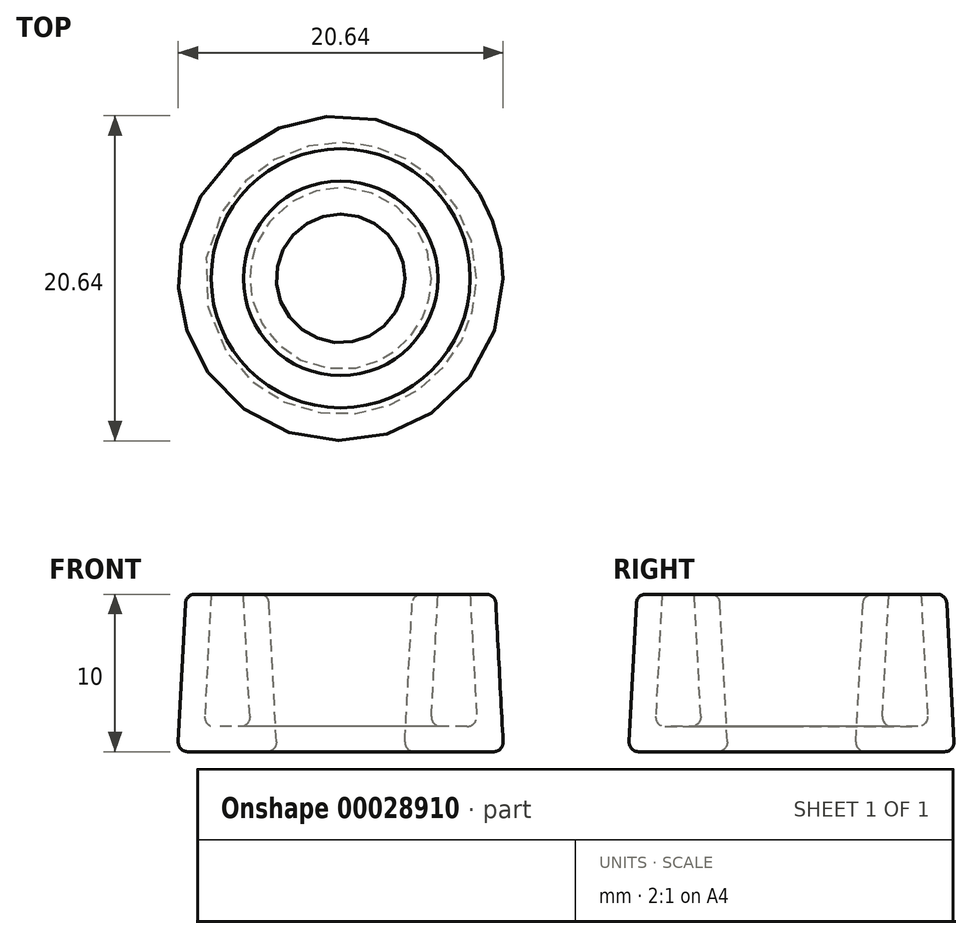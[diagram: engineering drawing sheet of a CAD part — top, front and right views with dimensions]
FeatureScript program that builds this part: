
annotation { "Feature Type Name" : "Feature", "Feature Type Description" : "" }
export const myFeature = defineFeature(function(context is Context, id is Id, definition is map)
    precondition{}
    {
        {
            var Q0;
            Q0=qCreatedBy(makeId("Top.planeOp"),FACE);
            var sketch = newSketch(context, id + "F0", { "sketchPlane" : qUnion([Q0])});
            skCircle(sketch, "E0", {"center": v(0, -10.65) * mm, "radius": 10.35 * mm});
            skCircle(sketch, "E1", {"center": v(0, -10.65) * mm, "radius": 4.05 * mm});
            skSolve(sketch);
        }
        {
            var Q0;
            Q0=makeQuery(id+"F0.imprint","IMPRINT",FACE,{"disambiguationData":[TD([[makeQuery(id+"F0.imprint","IMPRINT",EDGE,{"derivedFrom":sQuery(id+"F0.wireOp",EDGE,"e6d2bad5-9e76-4b41-926a-4b8b29525619")}),1.0]])]});
            var Q1;
            Q1=makeQuery(id+"F0.imprint","IMPRINT",FACE,{"disambiguationData":[TD([[makeQuery(id+"F0.imprint","IMPRINT",EDGE,{"derivedFrom":sQuery(id+"F0.wireOp",EDGE,"E0")}),1.0]])]});
            var Q2;
            Q2=makeQuery(id+"F0.imprint","IMPRINT",FACE,{"disambiguationData":[TD([[makeQuery(id+"F0.imprint","IMPRINT",EDGE,{"derivedFrom":sQuery(id+"F0.wireOp",EDGE,"abde0cf9-1f83-4301-beb9-ac4b5f17cbbd.bottom")}),1.0]])]});
            var Q3;
            Q3=makeQuery(id+"F0.imprint","IMPRINT",FACE,{"disambiguationData":[TD([[makeQuery(id+"F0.imprint","IMPRINT",EDGE,{"derivedFrom":sQuery(id+"F0.wireOp",EDGE,"26bd8618-c4e7-439a-99f6-bb982ce9a2120.MirrorC")}),-1.0]])]});
            var Q4;
            Q4=makeQuery(id+"F0.imprint","IMPRINT",FACE,{"disambiguationData":[TD([[makeQuery(id+"F0.imprint","IMPRINT",EDGE,{"derivedFrom":sQuery(id+"F0.wireOp",EDGE,"45c0c035-0ba1-440d-91dd-f4deb18173680.MirrorC")}),-1.0]])]});
            var Q5;
            Q5=makeQuery(id+"F0.imprint","IMPRINT",FACE,{"disambiguationData":[TD([[makeQuery(id+"F0.imprint","IMPRINT",EDGE,{"derivedFrom":sQuery(id+"F0.wireOp",EDGE,"92f10646-9b55-488a-b265-364474158b900.MirrorCS")}),1.0]])]});
            var Q6;
            {var subQ4=sQuery(id+"F0.wireOp",EDGE,"621f7957-7ed0-4eb6-82c1-ad9769d9a6c72.MirrorCS");Q6=makeQuery(id+"F0.imprint","IMPRINT",FACE,{"disambiguationData":[TD([[makeQuery(id+"F0.imprint","IMPRINT",EDGE,{"derivedFrom":subQ4}),-1.0]])]});}
            var Q7;
            Q7=makeQuery(id+"F0.imprint","IMPRINT",FACE,{"disambiguationData":[TD([[makeQuery(id+"F0.imprint","IMPRINT",EDGE,{"derivedFrom":sQuery(id+"F0.wireOp",EDGE,"621f7957-7ed0-4eb6-82c1-ad9769d9a6c70.MirrorCS")}),-1.0]])]});
            var Q8;
            Q8=makeQuery(id+"F0.imprint","IMPRINT",FACE,{"disambiguationData":[TD([[makeQuery(id+"F0.imprint","IMPRINT",EDGE,{"derivedFrom":sQuery(id+"F0.wireOp",EDGE,"621f7957-7ed0-4eb6-82c1-ad9769d9a6c78.MirrorCS")}),1.0]])]});
            var Q9;
            {var subQ4=sQuery(id+"F0.wireOp",EDGE,"621f7957-7ed0-4eb6-82c1-ad9769d9a6c72.MirrorCS");Q9=makeQuery(id+"F0.imprint","IMPRINT",FACE,{"disambiguationData":[TD([[makeQuery(id+"F0.imprint","IMPRINT",EDGE,{"derivedFrom":subQ4}),1.0]])]});}
            var Q10;
            Q10=makeQuery(id+"F0.imprint","IMPRINT",FACE,{"disambiguationData":[TD([[makeQuery(id+"F0.imprint","IMPRINT",EDGE,{"derivedFrom":sQuery(id+"F0.wireOp",EDGE,"0d3d05c0-9ec0-42d6-8d1c-98659f42b2b8.bottom")}),1.0]])]});
            var Q11;
            Q11=makeQuery(id+"F0.imprint","IMPRINT",FACE,{"disambiguationData":[TD([[makeQuery(id+"F0.imprint","IMPRINT",EDGE,{"derivedFrom":sQuery(id+"F0.wireOp",EDGE,"0d3d05c0-9ec0-42d6-8d1c-98659f42b2b8.bottom")}),1.0]])]});
            extrude(context, id + "F1", {"entities" : qUnion([Q0, Q1, Q2, Q3, Q4, Q5, Q6, Q7, Q8, Q9, Q10, Q11]), "depth" : 10 * mm, "hasDraft" : true, "draftAngle" : 3 * degree, "draftPullDirection" : true});
        }
        {
            var Q0;
            Q0=makeQuery(id+"F1.opExtrude","CAP_FACE",FACE,{"disambiguationData":[OSD([sQuery(id+"F0.wireOp",EDGE,"e6d2bad5-9e76-4b41-926a-4b8b29525619"),sQuery(id+"F0.wireOp",EDGE,"27f1a8c6-9d11-4593-bfca-9de2c4382994")])],"isStart":false});
            var Q1;
            Q1=makeQuery(id+"F1.opExtrude","CAP_FACE",FACE,{"disambiguationData":[OSD([sQuery(id+"F0.wireOp",EDGE,"b8262d11-0ced-4fc4-a484-381bc9a378e90.MirrorC"),sQuery(id+"F0.wireOp",EDGE,"9f1c5b67-5bd7-481e-852a-bcdd96d4567a0.MirrorC")])],"isStart":false});
            var Q2;
            Q2=makeQuery(id+"F1.opExtrude","CAP_FACE",FACE,{"disambiguationData":[OSD([sQuery(id+"F0.wireOp",EDGE,"E0"),sQuery(id+"F0.wireOp",EDGE,"E1")])],"isStart":false});
            var Q3;
            Q3=makeQuery(id+"F1.opExtrude","CAP_FACE",FACE,{"disambiguationData":[OSD([sQuery(id+"F0.wireOp",EDGE,"abde0cf9-1f83-4301-beb9-ac4b5f17cbbd.bottom"),sQuery(id+"F0.wireOp",EDGE,"abde0cf9-1f83-4301-beb9-ac4b5f17cbbd.top"),sQuery(id+"F0.wireOp",EDGE,"abde0cf9-1f83-4301-beb9-ac4b5f17cbbd.left"),sQuery(id+"F0.wireOp",EDGE,"abde0cf9-1f83-4301-beb9-ac4b5f17cbbd.right"),sQuery(id+"F0.wireOp",EDGE,"7a9050d6-7617-46cd-b5c2-3b15425381b2"),sQuery(id+"F0.wireOp",EDGE,"b158f154-8a0c-48af-83f9-a2040f8c14ea"),sQuery(id+"F0.wireOp",EDGE,"6b9fe175-4e1e-497c-82d7-d758e1c653ef.filletArc"),sQuery(id+"F0.wireOp",EDGE,"f33478da-a012-4289-b0bd-afe5d81a5774.filletArc"),sQuery(id+"F0.wireOp",EDGE,"24f43b8c-777b-4e50-8554-e1c6360b9280.filletArc"),sQuery(id+"F0.wireOp",EDGE,"1f811094-0bca-45d6-932f-2b620bfc63b1.filletArc")])],"isStart":false});
            var Q4;
            Q4=makeQuery(id+"F1.opExtrude","CAP_FACE",FACE,{"disambiguationData":[OSD([sQuery(id+"F0.wireOp",EDGE,"92f10646-9b55-488a-b265-364474158b900.MirrorCS"),sQuery(id+"F0.wireOp",EDGE,"92f10646-9b55-488a-b265-364474158b901.MirrorCS"),sQuery(id+"F0.wireOp",EDGE,"92f10646-9b55-488a-b265-364474158b902.MirrorCS"),sQuery(id+"F0.wireOp",EDGE,"92f10646-9b55-488a-b265-364474158b903.MirrorCS"),sQuery(id+"F0.wireOp",EDGE,"92f10646-9b55-488a-b265-364474158b904.MirrorC"),sQuery(id+"F0.wireOp",EDGE,"92f10646-9b55-488a-b265-364474158b905.MirrorC"),sQuery(id+"F0.wireOp",EDGE,"92f10646-9b55-488a-b265-364474158b909.MirrorCS"),sQuery(id+"F0.wireOp",EDGE,"92f10646-9b55-488a-b265-364474158b9010.MirrorCS"),sQuery(id+"F0.wireOp",EDGE,"92f10646-9b55-488a-b265-364474158b9011.MirrorCS"),sQuery(id+"F0.wireOp",EDGE,"92f10646-9b55-488a-b265-364474158b9012.MirrorCS")])],"isStart":false});
            var Q5;
            Q5=makeQuery(id+"F1.opExtrude","CAP_FACE",FACE,{"disambiguationData":[OSD([sQuery(id+"F0.wireOp",EDGE,"26bd8618-c4e7-439a-99f6-bb982ce9a2120.MirrorC"),sQuery(id+"F0.wireOp",EDGE,"a178782d-5131-49dc-9e23-0d626eec303c0.MirrorC")])],"isStart":false});
            var Q6;
            Q6=makeQuery(id+"F1.opExtrude","CAP_FACE",FACE,{"disambiguationData":[OSD([sQuery(id+"F0.wireOp",EDGE,"45c0c035-0ba1-440d-91dd-f4deb18173680.MirrorC"),sQuery(id+"F0.wireOp",EDGE,"d4880a5e-9c01-4a5a-914c-df641b7b912d0.MirrorC")])],"isStart":false});
            shell(context, id + "F2", {"entities" : qUnion([Q0, Q1, Q2, Q3, Q4, Q5, Q6]), "thickness" : 1.6 * mm});
        }
        {
            var Q0;
            Q0=makeQuery(id+"F1.opExtrude","SWEPT_FACE",FACE,{"disambiguationData":[OSD([sQuery(id+"F0.wireOp",EDGE,"26bd8618-c4e7-439a-99f6-bb982ce9a2120.MirrorC")])]});
            var Q1;
            Q1=makeQuery(id+"F1.opExtrude","SWEPT_FACE",FACE,{"disambiguationData":[OSD([sQuery(id+"F0.wireOp",EDGE,"e6d2bad5-9e76-4b41-926a-4b8b29525619")])]});
            var Q2;
            {var subQ0=sQuery(id+"F0.wireOp",EDGE,"e6d2bad5-9e76-4b41-926a-4b8b29525619");var subQ1=sQuery(id+"F0.wireOp",EDGE,"27f1a8c6-9d11-4593-bfca-9de2c4382994");Q2=makeQuery(id+"F2.opShell","OFFSET_FACE",FACE,{"disambiguationData":[OSD([subQ0,subQ1]),TDD([makeQuery(id+"F1.opExtrude","CAP_FACE",FACE,{"disambiguationData":[OSD([subQ0,subQ1])],"isStart":true})])]});}
            var Q3;
            {var subQ0=sQuery(id+"F0.wireOp",EDGE,"26bd8618-c4e7-439a-99f6-bb982ce9a2120.MirrorC");var subQ1=sQuery(id+"F0.wireOp",EDGE,"a178782d-5131-49dc-9e23-0d626eec303c0.MirrorC");Q3=makeQuery(id+"F2.opShell","OFFSET_FACE",FACE,{"disambiguationData":[OSD([subQ0,subQ1]),TDD([makeQuery(id+"F1.opExtrude","CAP_FACE",FACE,{"disambiguationData":[OSD([subQ0,subQ1])],"isStart":true})])]});}
            var Q4;
            {var subQ0=sQuery(id+"F0.wireOp",EDGE,"45c0c035-0ba1-440d-91dd-f4deb18173680.MirrorC");var subQ1=sQuery(id+"F0.wireOp",EDGE,"d4880a5e-9c01-4a5a-914c-df641b7b912d0.MirrorC");Q4=makeQuery(id+"F2.opShell","OFFSET_FACE",FACE,{"disambiguationData":[OSD([subQ0,subQ1]),TDD([makeQuery(id+"F1.opExtrude","CAP_FACE",FACE,{"disambiguationData":[OSD([subQ0,subQ1])],"isStart":true})])]});}
            var Q5;
            {var subQ0=sQuery(id+"F0.wireOp",EDGE,"E0");var subQ1=sQuery(id+"F0.wireOp",EDGE,"E1");Q5=makeQuery(id+"F2.opShell","OFFSET_FACE",FACE,{"disambiguationData":[OSD([subQ0,subQ1]),TDD([makeQuery(id+"F1.opExtrude","CAP_FACE",FACE,{"disambiguationData":[OSD([subQ0,subQ1])],"isStart":true})])]});}
            var Q6;
            Q6=makeQuery(id+"F1.opExtrude","SWEPT_FACE",FACE,{"disambiguationData":[OSD([sQuery(id+"F0.wireOp",EDGE,"92f10646-9b55-488a-b265-364474158b909.MirrorCS")])]});
            var Q7;
            Q7=makeQuery(id+"F1.opExtrude","CAP_EDGE",EDGE,{"disambiguationData":[OSD([sQuery(id+"F0.wireOp",EDGE,"E1")])],"isStart":false});
            var Q8;
            Q8=makeQuery(id+"F1.opExtrude","CAP_EDGE",EDGE,{"disambiguationData":[OSD([sQuery(id+"F0.wireOp",EDGE,"d4880a5e-9c01-4a5a-914c-df641b7b912d0.MirrorC")])],"isStart":false});
            var Q9;
            Q9=makeQuery(id+"F1.opExtrude","SWEPT_FACE",FACE,{"disambiguationData":[OSD([sQuery(id+"F0.wireOp",EDGE,"abde0cf9-1f83-4301-beb9-ac4b5f17cbbd.right")])]});
            var Q10;
            Q10=makeQuery(id+"F1.opExtrude","CAP_EDGE",EDGE,{"disambiguationData":[OSD([sQuery(id+"F0.wireOp",EDGE,"45c0c035-0ba1-440d-91dd-f4deb18173680.MirrorC")])],"isStart":false});
            var Q11;
            Q11=makeQuery(id+"F1.opExtrude","CAP_EDGE",EDGE,{"disambiguationData":[OSD([sQuery(id+"F0.wireOp",EDGE,"E0")])],"isStart":false});
            var Q12;
            {var subQ0=sQuery(id+"F0.wireOp",EDGE,"92f10646-9b55-488a-b265-364474158b900.MirrorCS");var subQ1=sQuery(id+"F0.wireOp",EDGE,"92f10646-9b55-488a-b265-364474158b901.MirrorCS");var subQ2=sQuery(id+"F0.wireOp",EDGE,"92f10646-9b55-488a-b265-364474158b902.MirrorCS");var subQ3=sQuery(id+"F0.wireOp",EDGE,"92f10646-9b55-488a-b265-364474158b903.MirrorCS");var subQ4=sQuery(id+"F0.wireOp",EDGE,"92f10646-9b55-488a-b265-364474158b904.MirrorC");var subQ5=sQuery(id+"F0.wireOp",EDGE,"92f10646-9b55-488a-b265-364474158b905.MirrorC");var subQ6=sQuery(id+"F0.wireOp",EDGE,"92f10646-9b55-488a-b265-364474158b909.MirrorCS");var subQ7=sQuery(id+"F0.wireOp",EDGE,"92f10646-9b55-488a-b265-364474158b9010.MirrorCS");var subQ8=sQuery(id+"F0.wireOp",EDGE,"92f10646-9b55-488a-b265-364474158b9011.MirrorCS");var subQ9=sQuery(id+"F0.wireOp",EDGE,"92f10646-9b55-488a-b265-364474158b9012.MirrorCS");Q12=makeQuery(id+"F2.opShell","OFFSET_FACE",FACE,{"disambiguationData":[OSD([subQ0,subQ1,subQ2,subQ3,subQ4,subQ5,subQ6,subQ7,subQ8,subQ9]),TDD([makeQuery(id+"F1.opExtrude","CAP_FACE",FACE,{"disambiguationData":[OSD([subQ0,subQ1,subQ2,subQ3,subQ4,subQ5,subQ6,subQ7,subQ8,subQ9])],"isStart":true})])]});}
            var Q13;
            {var subQ0=sQuery(id+"F0.wireOp",EDGE,"abde0cf9-1f83-4301-beb9-ac4b5f17cbbd.bottom");var subQ1=sQuery(id+"F0.wireOp",EDGE,"abde0cf9-1f83-4301-beb9-ac4b5f17cbbd.top");var subQ2=sQuery(id+"F0.wireOp",EDGE,"abde0cf9-1f83-4301-beb9-ac4b5f17cbbd.left");var subQ3=sQuery(id+"F0.wireOp",EDGE,"abde0cf9-1f83-4301-beb9-ac4b5f17cbbd.right");var subQ4=sQuery(id+"F0.wireOp",EDGE,"7a9050d6-7617-46cd-b5c2-3b15425381b2");var subQ5=sQuery(id+"F0.wireOp",EDGE,"b158f154-8a0c-48af-83f9-a2040f8c14ea");var subQ6=sQuery(id+"F0.wireOp",EDGE,"6b9fe175-4e1e-497c-82d7-d758e1c653ef.filletArc");var subQ7=sQuery(id+"F0.wireOp",EDGE,"f33478da-a012-4289-b0bd-afe5d81a5774.filletArc");var subQ8=sQuery(id+"F0.wireOp",EDGE,"24f43b8c-777b-4e50-8554-e1c6360b9280.filletArc");var subQ9=sQuery(id+"F0.wireOp",EDGE,"1f811094-0bca-45d6-932f-2b620bfc63b1.filletArc");Q13=makeQuery(id+"F2.opShell","OFFSET_FACE",FACE,{"disambiguationData":[OSD([subQ0,subQ1,subQ2,subQ3,subQ4,subQ5,subQ6,subQ7,subQ8,subQ9]),TDD([makeQuery(id+"F1.opExtrude","CAP_FACE",FACE,{"disambiguationData":[OSD([subQ0,subQ1,subQ2,subQ3,subQ4,subQ5,subQ6,subQ7,subQ8,subQ9])],"isStart":true})])]});}
            var Q14;
            Q14=makeQuery(id+"F1.opExtrude","CAP_EDGE",EDGE,{"disambiguationData":[OSD([sQuery(id+"F0.wireOp",EDGE,"E0")])],"isStart":true});
            var Q15;
            Q15=makeQuery(id+"F1.opExtrude","CAP_EDGE",EDGE,{"disambiguationData":[OSD([sQuery(id+"F0.wireOp",EDGE,"E1")])],"isStart":true});
            fillet(context, id + "F3", {"entities" : qUnion([Q0, Q1, Q2, Q3, Q4, Q5, Q6, Q7, Q8, Q9, Q10, Q11, Q12, Q13, Q14, Q15]), "radius" : 0.6 * mm, "tangentPropagation" : true, "allowEdgeOverflow" : false});
        }
    });
